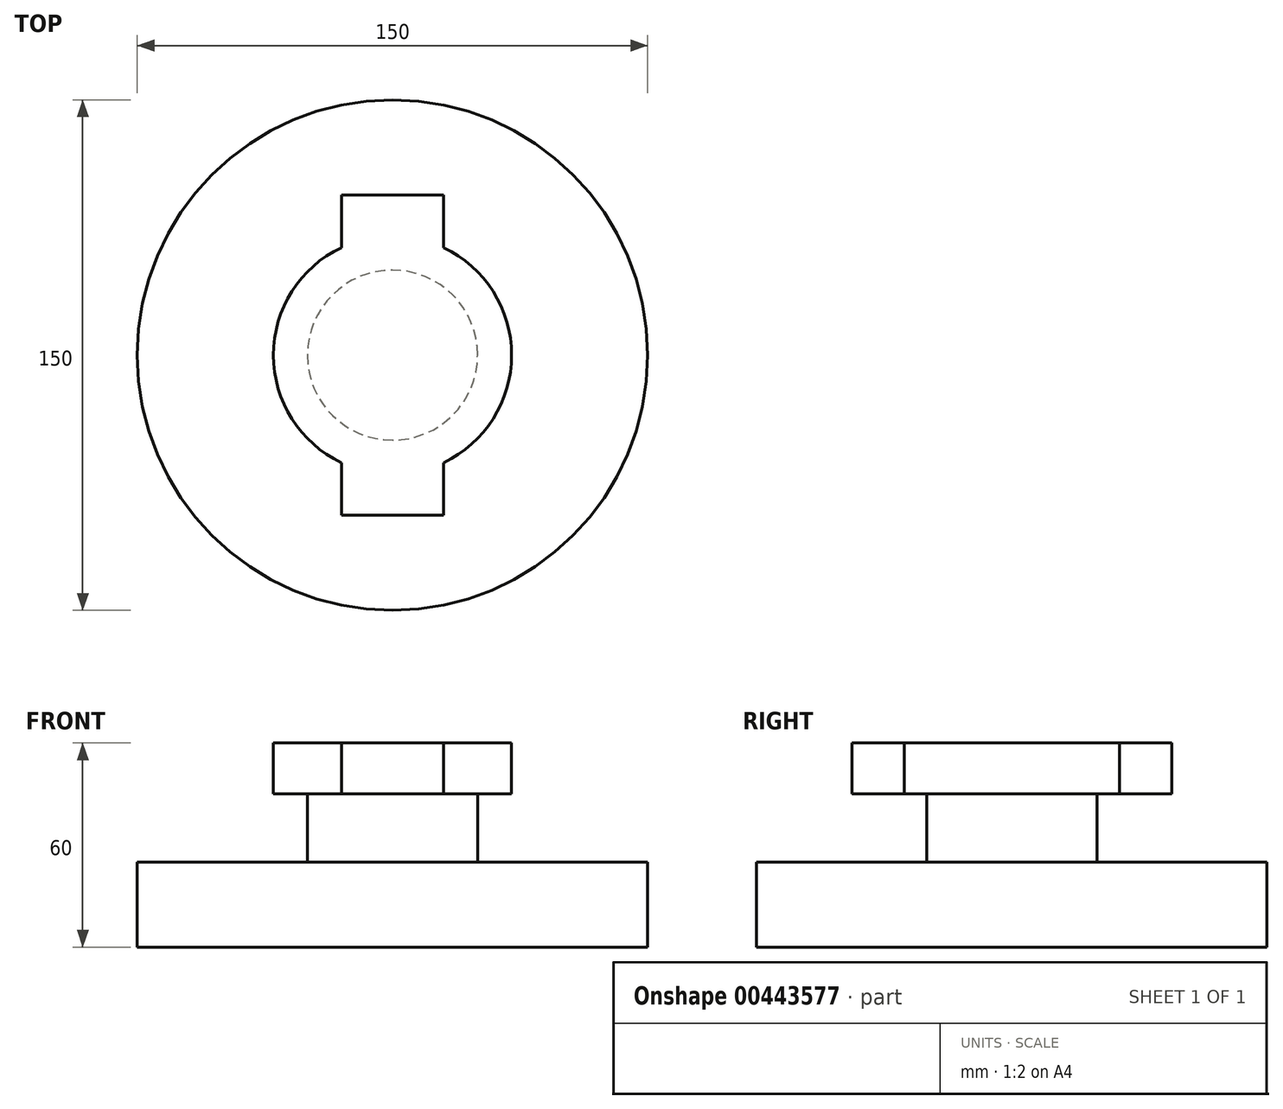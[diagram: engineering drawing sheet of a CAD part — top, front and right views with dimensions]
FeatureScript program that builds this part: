
annotation { "Feature Type Name" : "Feature", "Feature Type Description" : "" }
export const myFeature = defineFeature(function(context is Context, id is Id, definition is map)
    precondition{}
    {
        {
            var Q0;
            Q0=qCreatedBy(makeId("Top.planeOp"),FACE);
            var sketch = newSketch(context, id + "F0", { "sketchPlane" : qUnion([Q0])});
            skCircle(sketch, "E0", {"center": v(0, 0) * mm, "radius": 35 * mm});
            skLineSegment(sketch, "E1.bottom", {"start": v(-15, 47) * mm, "end": v(15, 47) * mm});
            skLineSegment(sketch, "E1.top", {"start": v(-15, 27.5) * mm, "end": v(15, 27.5) * mm});
            skLineSegment(sketch, "E1.left", {"start": v(-15, 47) * mm, "end": v(-15, 27.5) * mm});
            skLineSegment(sketch, "E1.right", {"start": v(15, 47) * mm, "end": v(15, 27.5) * mm});
            skLineSegment(sketch, "E2.bottom", {"start": v(-15, -27.5) * mm, "end": v(15, -27.5) * mm});
            skLineSegment(sketch, "E2.top", {"start": v(-15, -47) * mm, "end": v(15, -47) * mm});
            skLineSegment(sketch, "E2.left", {"start": v(-15, -27.5) * mm, "end": v(-15, -47) * mm});
            skLineSegment(sketch, "E2.right", {"start": v(15, -27.5) * mm, "end": v(15, -47) * mm});
            skSolve(sketch);
        }
        {
            var Q0;
            Q0 = qSketchRegion(id + "F0", true);
            extrude(context, id + "F1", {"entities" : qUnion([Q0]), "depth" : 15 * mm});
        }
        {
            var Q0;
            Q0=qCreatedBy(makeId("Top.planeOp"),FACE);
            var sketch = newSketch(context, id + "F2", { "sketchPlane" : qUnion([Q0])});
            skCircle(sketch, "E3", {"center": v(0, 0) * mm, "radius": 25 * mm});
            skSolve(sketch);
        }
        {
            var Q0;
            Q0 = qSketchRegion(id + "F2", true);
            extrude(context, id + "F3", {"entities" : qUnion([Q0]), "operationType" : NewBodyOperationType.ADD, "oppositeDirection" : true, "depth" : 20 * mm});
        }
        {
            var Q0;
            Q0=qCreatedBy(makeId("Top.planeOp"),FACE);
            cPlane(context, id + "F4", {"entities" : qUnion([Q0]), "cplaneType" : CPlaneType.OFFSET, "offset" : 20 * mm, "oppositeDirection" : true, "width" : 150 * mm, "height" : 150 * mm});
        }
        {
            var Q0;
            Q0=qCreatedBy(id+"F4.planeOp",FACE);
            var sketch = newSketch(context, id + "F5", { "sketchPlane" : qUnion([Q0])});
            skCircle(sketch, "E4", {"center": v(0, 0) * mm, "radius": 75 * mm});
            skSolve(sketch);
        }
        {
            var Q0;
            Q0 = qSketchRegion(id + "F5", true);
            extrude(context, id + "F6", {"entities" : qUnion([Q0]), "operationType" : NewBodyOperationType.ADD, "oppositeDirection" : true, "depth" : 25 * mm});
        }
    });
